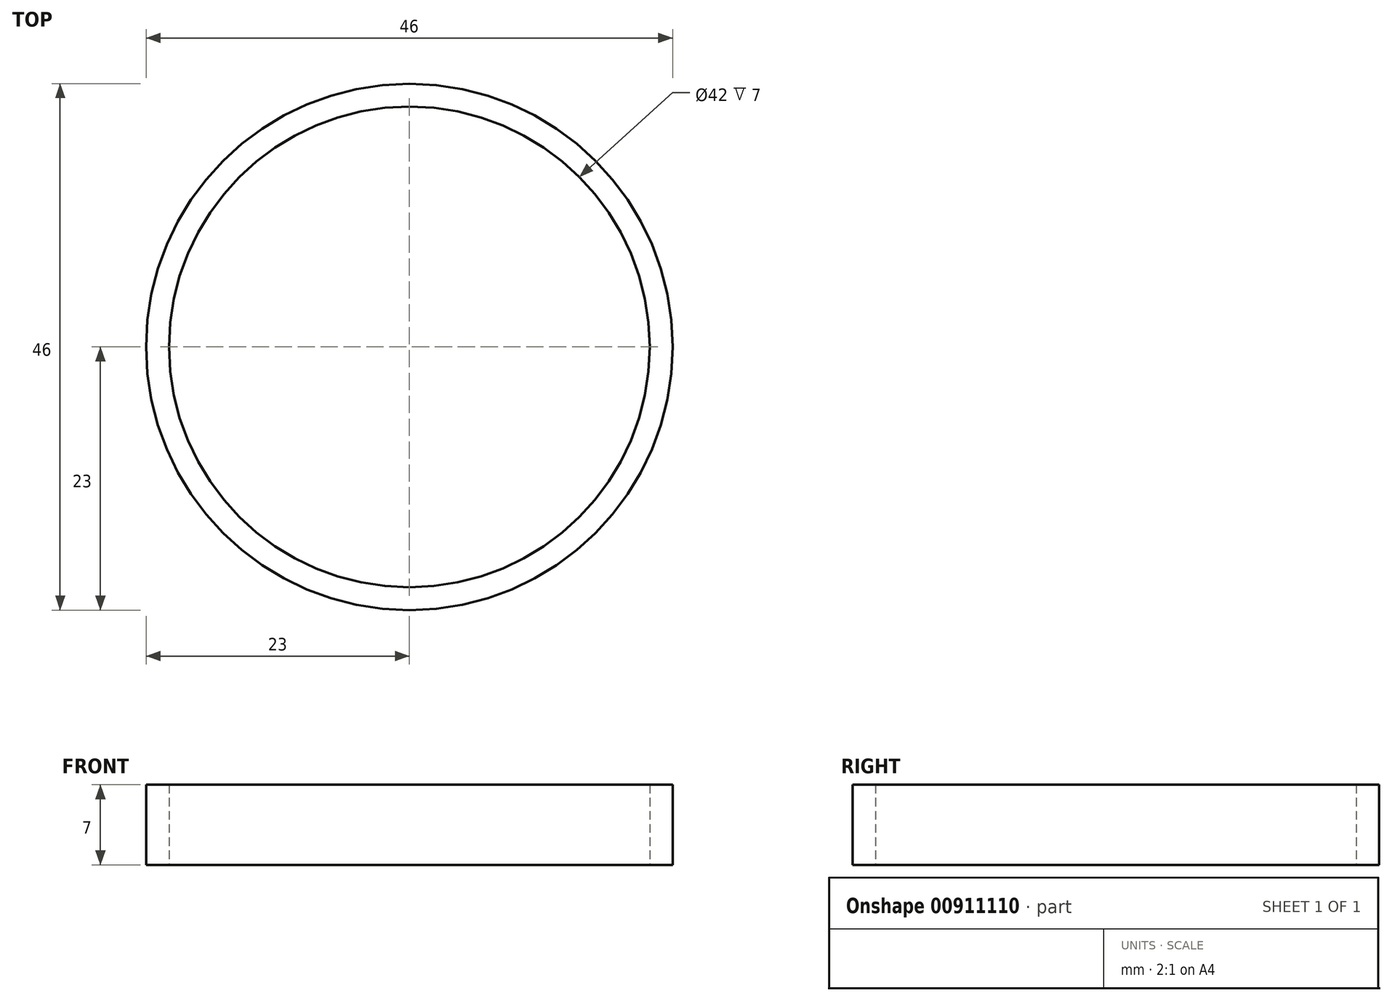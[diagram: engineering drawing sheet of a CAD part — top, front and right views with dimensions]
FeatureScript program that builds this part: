
annotation { "Feature Type Name" : "Feature", "Feature Type Description" : "" }
export const myFeature = defineFeature(function(context is Context, id is Id, definition is map)
    precondition{}
    {
        {
            var Q0;
            Q0=qCreatedBy(makeId("Top.planeOp"),FACE);
            var sketch = newSketch(context, id + "F0", { "sketchPlane" : qUnion([Q0])});
            skCircle(sketch, "E0", {"center": v(0, 0) * mm, "radius": 21 * mm});
            skCircle(sketch, "E1", {"center": v(0, 0) * mm, "radius": 23 * mm});
            skSolve(sketch);
        }
        {
            var Q0;
            Q0 = qSketchRegion(id + "F0", true);
            extrude(context, id + "F1", {"entities" : qUnion([Q0]), "depth" : 7 * mm, "offsetDistance" : 25 * mm});
        }
    });
